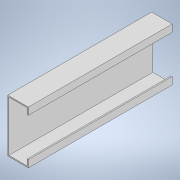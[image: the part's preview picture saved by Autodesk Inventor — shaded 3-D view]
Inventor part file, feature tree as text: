
AUTODESK INVENTOR PART (.ipt)
format: ipt  version: 2020 (Build 240168000, 168)  size: 107,008 bytes
history: native  units: mm
features: extrude x1, sketch x1
ambient origin geometry x8: Origin, YZ Plane, XZ Plane, XY Plane, X Axis, Y Axis, Z Axis, Center Point
bodies: Solid1 (feature_tree)
feature tree (2):
  extrude  "Extrusion1"  Depth=110.0mm
  sketch  "Sketch1"  dims[d0=43.0mm d1=110.0mm d2=15.0mm d3=15.0mm d4=2.5mm d5=300.0mm d6=0.0mm]
